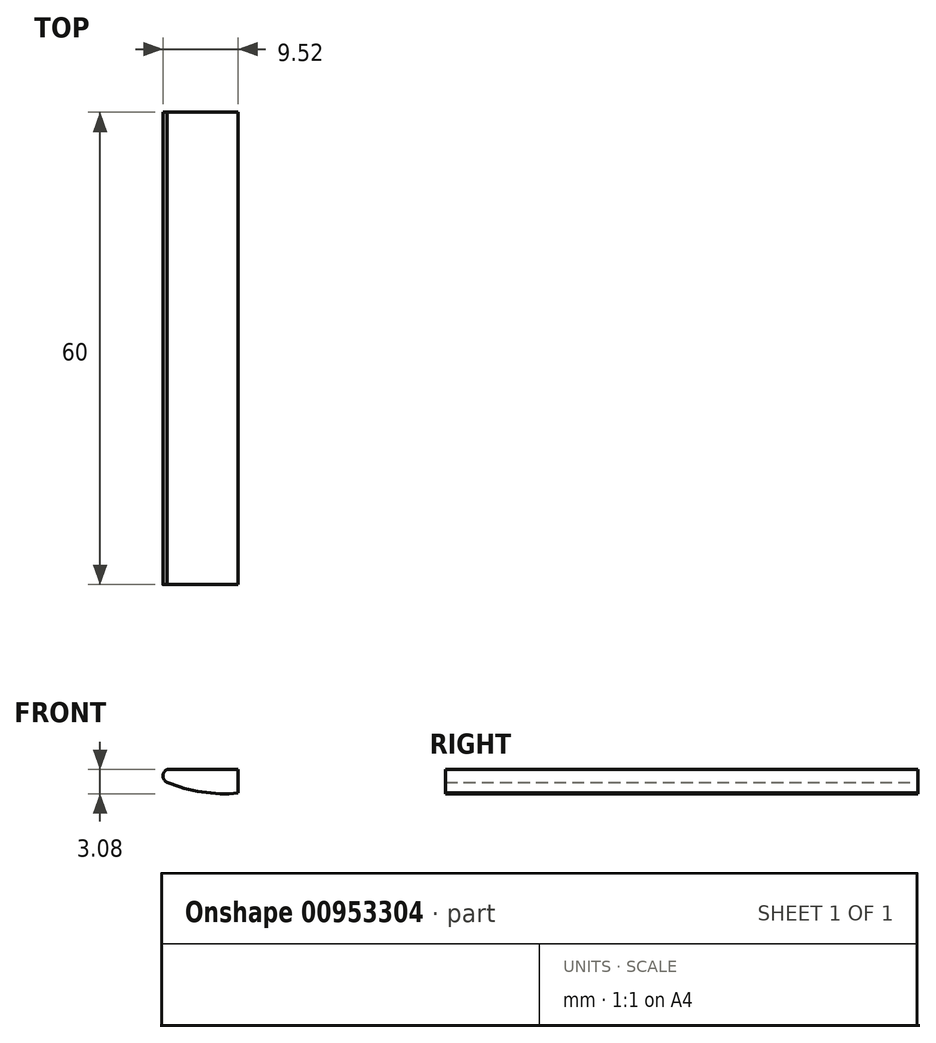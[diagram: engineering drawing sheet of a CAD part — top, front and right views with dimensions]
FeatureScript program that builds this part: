
annotation { "Feature Type Name" : "Feature", "Feature Type Description" : "" }
export const myFeature = defineFeature(function(context is Context, id is Id, definition is map)
    precondition{}
    {
        {
            var Q0;
            Q0=qCreatedBy(makeId("Front.planeOp"),FACE);
            var sketch = newSketch(context, id + "F0", { "sketchPlane" : qUnion([Q0])});
            skLineSegment(sketch, "E0", {"start": v(0, 0) * mm, "end": v(0, 3) * mm});
            skLineSegment(sketch, "E1", {"start": v(0, 3) * mm, "end": v(-9, 3) * mm});
            skArc(sketch, "E2", {"start": v(-9, 1.37) * mm, "mid": v(-4.58, 0.14) * mm, "end": v(0, 0) * mm});
            skArc(sketch, "E3", {"start": v(-9, 3) * mm, "mid": v(-9.52, 2.18) * mm, "end": v(-9, 1.37) * mm});
            skSolve(sketch);
        }
        {
            var Q0;
            Q0=makeQuery(id+"F0.imprint","IMPRINT",FACE,{"disambiguationData":[TD([[makeQuery(id+"F0.imprint","IMPRINT",EDGE,{"derivedFrom":sQuery(id+"F0.wireOp",EDGE,"E0")}),1.0]])]});
            extrude(context, id + "F1", {"entities" : qUnion([Q0]), "depth" : 60 * mm, "offsetDistance" : 25 * mm});
        }
    });
